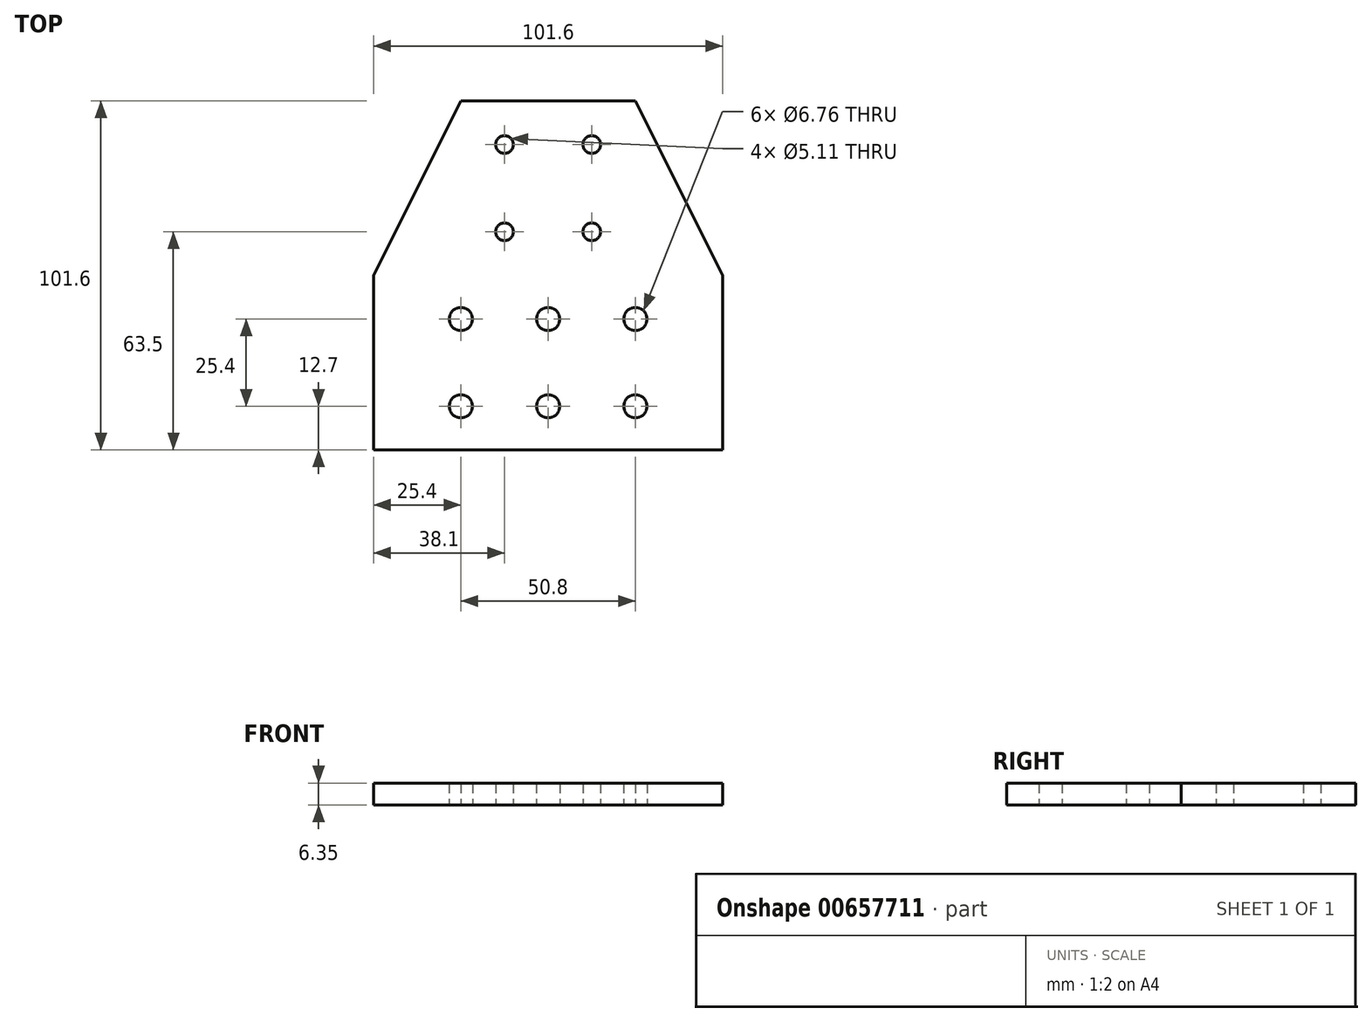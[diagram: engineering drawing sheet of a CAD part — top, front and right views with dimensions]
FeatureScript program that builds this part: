
annotation { "Feature Type Name" : "Feature", "Feature Type Description" : "" }
export const myFeature = defineFeature(function(context is Context, id is Id, definition is map)
    precondition{}
    {
        {
            var Q0;
            Q0=qCreatedBy(makeId("Top.planeOp"),FACE);
            var sketch = newSketch(context, id + "F0", { "sketchPlane" : qUnion([Q0])});
            skLineSegment(sketch, "E0.bottom", {"start": v(0, 0) * mm, "end": v(101.6, 0) * mm});
            skLineSegment(sketch, "E0.top", {"start": v(0, -101.6) * mm, "end": v(101.6, -101.6) * mm});
            skLineSegment(sketch, "E0.left", {"start": v(0, 0) * mm, "end": v(0, -101.6) * mm});
            skLineSegment(sketch, "E0.right", {"start": v(101.6, 0) * mm, "end": v(101.6, -101.6) * mm});
            skLineSegment(sketch, "E1", {"start": v(25.4, 0) * mm, "end": v(0, -50.8) * mm});
            skLineSegment(sketch, "E2", {"start": v(76.2, 0) * mm, "end": v(101.6, -50.8) * mm});
            skCircle(sketch, "E3", {"center": v(38.1, -12.7) * mm, "radius": 2.55 * mm});
            skCircle(sketch, "E4.0.1.0", {"center": v(38.1, -38.1) * mm, "radius": 2.55 * mm});
            skCircle(sketch, "E4.1.0.0", {"center": v(63.5, -12.7) * mm, "radius": 2.55 * mm});
            skCircle(sketch, "E4.1.1.0", {"center": v(63.5, -38.1) * mm, "radius": 2.55 * mm});
            skLineSegment(sketch, "E4.direction1", {"start": v(38.1, -12.7) * mm, "end": v(63.5, -12.7) * mm, "construction": true});
            skLineSegment(sketch, "E4.direction2", {"start": v(38.1, -12.7) * mm, "end": v(38.1, -38.1) * mm, "construction": true});
            skCircle(sketch, "E5", {"center": v(25.4, -63.5) * mm, "radius": 3.38 * mm});
            skCircle(sketch, "E6.0.1.0", {"center": v(25.4, -88.9) * mm, "radius": 3.38 * mm});
            skCircle(sketch, "E6.1.0.0", {"center": v(50.8, -63.5) * mm, "radius": 3.38 * mm});
            skCircle(sketch, "E6.1.1.0", {"center": v(50.8, -88.9) * mm, "radius": 3.38 * mm});
            skCircle(sketch, "E6.2.0.0", {"center": v(76.2, -63.5) * mm, "radius": 3.38 * mm});
            skCircle(sketch, "E6.2.1.0", {"center": v(76.2, -88.9) * mm, "radius": 3.38 * mm});
            skLineSegment(sketch, "E6.direction1", {"start": v(25.4, -63.5) * mm, "end": v(50.8, -63.5) * mm, "construction": true});
            skLineSegment(sketch, "E6.direction2", {"start": v(25.4, -63.5) * mm, "end": v(25.4, -88.9) * mm, "construction": true});
            skSolve(sketch);
        }
        {
            var Q0;
            {var subQ3=sQuery(id+"F0.wireOp",EDGE,"E0.top");Q0=makeQuery(id+"F0.imprint","IMPRINT",FACE,{"disambiguationData":[TD([[makeQuery(id+"F0.imprint","IMPRINT",EDGE,{"derivedFrom":subQ3}),1.0]])]});}
            extrude(context, id + "F1", {"entities" : qUnion([Q0]), "depth" : 6.35 * mm, "offsetDistance" : 25.4 * mm});
        }
    });
